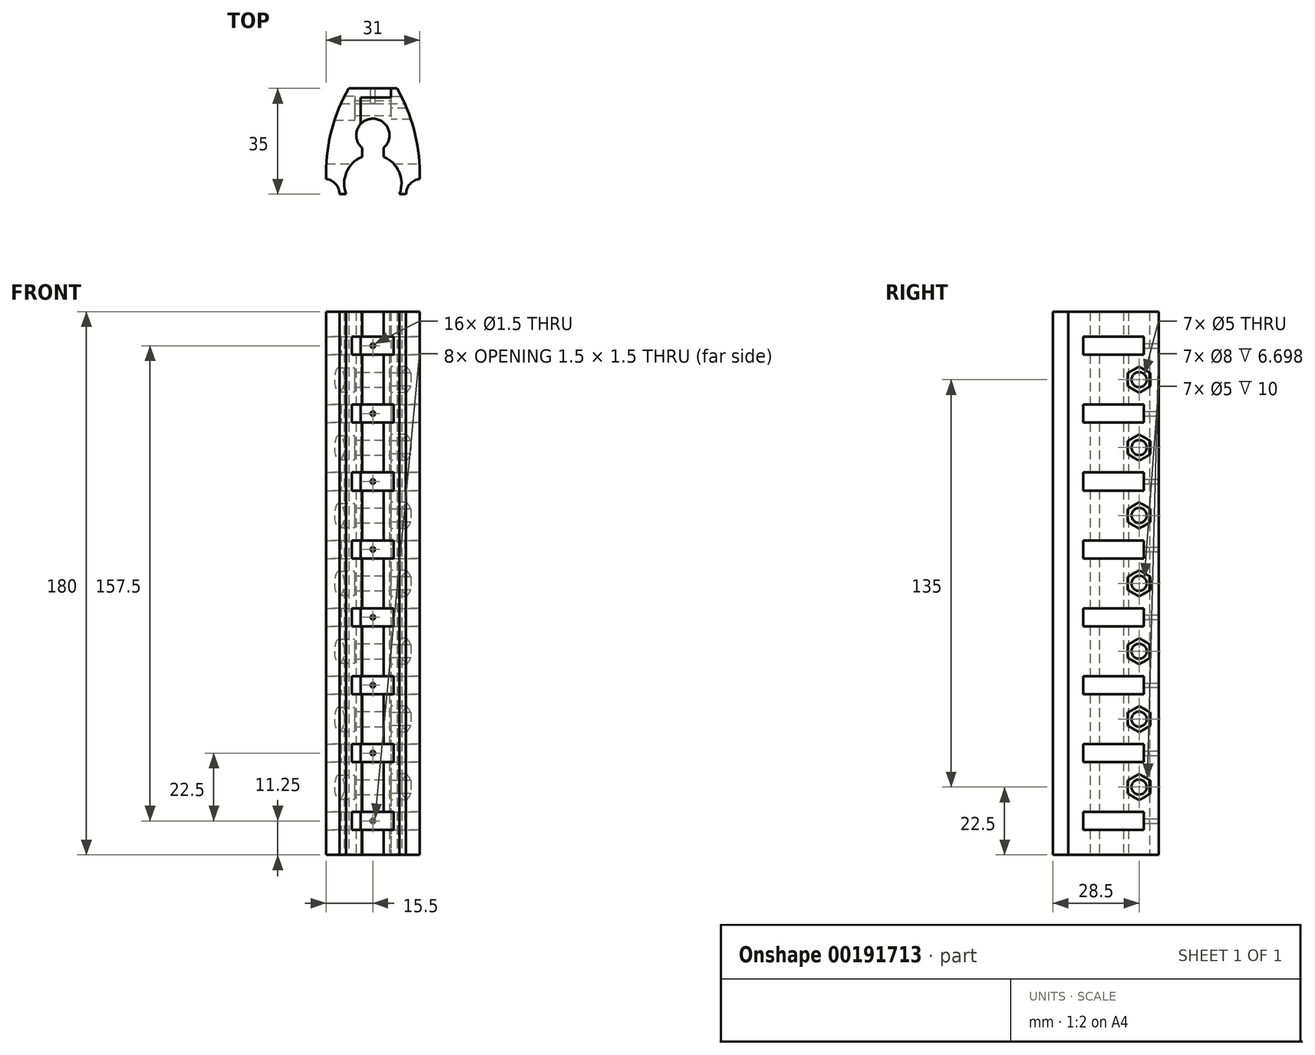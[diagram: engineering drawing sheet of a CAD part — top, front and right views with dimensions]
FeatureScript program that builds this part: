
annotation { "Feature Type Name" : "Feature", "Feature Type Description" : "" }
export const myFeature = defineFeature(function(context is Context, id is Id, definition is map)
    precondition{}
    {
        {
            var Q0;
            Q0=qCreatedBy(makeId("Top.planeOp"),FACE);
            var sketch = newSketch(context, id + "F0", { "sketchPlane" : qUnion([Q0])});
            skArc(sketch, "E0", {"start": v(3.56, -4.2) * mm, "mid": v(0, 5.5) * mm, "end": v(-3.56, -4.2) * mm});
            skArc(sketch, "E1", {"start": v(8.83, -19.5) * mm, "mid": v(8.73, -12.26) * mm, "end": v(3.56, -7.2) * mm});
            skLineSegment(sketch, "E2", {"start": v(-8.83, -19.5) * mm, "end": v(-11, -19.5) * mm});
            skLineSegment(sketch, "E3", {"start": v(-15.5, -14.53) * mm, "end": v(-15.5, -12.5) * mm});
            skLineSegment(sketch, "E4", {"start": v(-8, 15.5) * mm, "end": v(8, 15.5) * mm});
            skPoint(sketch, "E5", {"position": v(0, 15.5) * mm});
            skLineSegment(sketch, "E6", {"start": v(0, 30.37) * mm, "end": v(0, -34.56) * mm, "construction": true});
            skPoint(sketch, "E7", {"position": v(-15.5, -16) * mm});
            skArc(sketch, "E8", {"start": v(-8, 15.5) * mm, "mid": v(-13.6, 2) * mm, "end": v(-15.5, -12.5) * mm});
            skArc(sketch, "E9.MirrorCS", {"start": v(8, 15.5) * mm, "mid": v(13.6, 2) * mm, "end": v(15.5, -12.5) * mm});
            skLineSegment(sketch, "E10.MirrorCS", {"start": v(15.5, -14.53) * mm, "end": v(15.5, -12.5) * mm});
            skLineSegment(sketch, "E11.MirrorCS", {"start": v(8.83, -19.5) * mm, "end": v(11, -19.5) * mm});
            skLineSegment(sketch, "E12", {"start": v(-3.56, -4.2) * mm, "end": v(-3.56, -7.2) * mm});
            skLineSegment(sketch, "E13.MirrorCS", {"start": v(3.56, -4.2) * mm, "end": v(3.56, -7.2) * mm});
            skArc(sketch, "E14.trimOffspring", {"start": v(-3.56, -7.2) * mm, "mid": v(-8.73, -12.26) * mm, "end": v(-8.83, -19.5) * mm});
            skLineSegment(sketch, "E15", {"start": v(0, 15.5) * mm, "end": v(0, 5.5) * mm});
            skArc(sketch, "E16", {"start": v(-11, -19.5) * mm, "mid": v(-12.3, -16.15) * mm, "end": v(-15.5, -14.53) * mm});
            skArc(sketch, "E17", {"start": v(15.5, -14.53) * mm, "mid": v(12.3, -16.15) * mm, "end": v(11, -19.5) * mm});
            skPoint(sketch, "E18.orphan", {"position": v(15.5, -19.5) * mm});
            skPoint(sketch, "E19.orphan", {"position": v(-15.5, -19.5) * mm});
            skLineSegment(sketch, "E20", {"start": v(6, 15.5) * mm, "end": v(6, 12.5) * mm});
            skLineSegment(sketch, "E21", {"start": v(6, 12.5) * mm, "end": v(-4, 12.5) * mm});
            skLineSegment(sketch, "E22", {"start": v(-4, 12.5) * mm, "end": v(-4, 3.77) * mm});
            skSolve(sketch);
        }
        {
            var Q0;
            Q0=makeQuery(id+"F0.imprint","IMPRINT",FACE,{"disambiguationData":[TD([[makeQuery(id+"F0.imprint","IMPRINT",EDGE,{"derivedFrom":sQuery(id+"F0.wireOp",EDGE,"E1")}),-1.0]])]});
            var Q1;
            {var subQ3=sQuery(id+"F0.wireOp",EDGE,"E22");Q1=makeQuery(id+"F0.imprint","IMPRINT",FACE,{"disambiguationData":[TD([[makeQuery(id+"F0.imprint","IMPRINT",EDGE,{"derivedFrom":subQ3}),1.0]])]});}
            extrude(context, id + "F1", {"entities" : qUnion([Q0, Q1]), "depth" : 180 * mm});
        }
        {
            var Q0;
            Q0=makeQuery(id+"F0.imprint","IMPRINT",FACE,{"disambiguationData":[TD([[makeQuery(id+"F0.imprint","IMPRINT",EDGE,{"derivedFrom":sQuery(id+"F0.wireOp",EDGE,"E2")}),-1.0]])]});
            var Q1;
            {var subQ3=sQuery(id+"F0.wireOp",EDGE,"E20");Q1=makeQuery(id+"F0.imprint","IMPRINT",FACE,{"disambiguationData":[TD([[makeQuery(id+"F0.imprint","IMPRINT",EDGE,{"derivedFrom":subQ3}),-1.0]])]});}
            extrude(context, id + "F2", {"entities" : qUnion([Q0, Q1]), "depth" : 180 * mm});
        }
        {
            var Q0;
            Q0=qCreatedBy(makeId("Right.planeOp"),FACE);
            var sketch = newSketch(context, id + "F3", { "sketchPlane" : qUnion([Q0])});
            skCircle(sketch, "E23", {"center": v(9, 22.5) * mm, "radius": 2.5 * mm});
            skCircle(sketch, "E24", {"center": v(9, 45) * mm, "radius": 2.5 * mm});
            skCircle(sketch, "E25", {"center": v(9, 67.5) * mm, "radius": 2.5 * mm});
            skCircle(sketch, "E26", {"center": v(9, 90) * mm, "radius": 2.5 * mm});
            skCircle(sketch, "E27", {"center": v(9, 112.5) * mm, "radius": 2.5 * mm});
            skCircle(sketch, "E28", {"center": v(9, 135) * mm, "radius": 2.5 * mm});
            skCircle(sketch, "E29", {"center": v(9, 157.5) * mm, "radius": 2.5 * mm});
            skLineSegment(sketch, "E30", {"start": v(9, 22.5) * mm, "end": v(9, 157.5) * mm, "construction": true});
            skLineSegment(sketch, "E31", {"start": v(9, 90) * mm, "end": v(15.5, 90) * mm, "construction": true});
            skSolve(sketch);
        }
        {
            var Q0;
            Q0 = qSketchRegion(id + "F3", true);
            extrude(context, id + "F4", {"entities" : qUnion([Q0]), "operationType" : NewBodyOperationType.REMOVE, "endBound" : BoundingType.SYMMETRIC, "oppositeDirection" : true, "depth" : 100 * mm});
        }
        {
            var Q0;
            Q0=qCreatedBy(makeId("Right.planeOp"),FACE);
            var sketch = newSketch(context, id + "F5", { "sketchPlane" : qUnion([Q0])});
            skCircle(sketch, "E32", {"center": v(9, 22.5) * mm, "radius": 4 * mm});
            skCircle(sketch, "E33", {"center": v(9, 45) * mm, "radius": 4 * mm});
            skCircle(sketch, "E34", {"center": v(9, 67.5) * mm, "radius": 4 * mm});
            skCircle(sketch, "E35", {"center": v(9, 90) * mm, "radius": 4 * mm});
            skCircle(sketch, "E36", {"center": v(9, 112.5) * mm, "radius": 4 * mm});
            skCircle(sketch, "E37", {"center": v(9, 135) * mm, "radius": 4 * mm});
            skCircle(sketch, "E38", {"center": v(9, 157.5) * mm, "radius": 4 * mm});
            skSolve(sketch);
        }
        {
            var Q0;
            Q0 = qSketchRegion(id + "F5", true);
            extrude(context, id + "F6", {"entities" : qUnion([Q0]), "operationType" : NewBodyOperationType.REMOVE, "oppositeDirection" : true, "depth" : 45.7 * mm, "hasSecondDirection" : true, "secondDirectionOppositeDirection" : true, "secondDirectionDepth" : 6 * mm});
        }
        {
            var Q0;
            Q0=qCreatedBy(makeId("Right.planeOp"),FACE);
            var sketch = newSketch(context, id + "F7", { "sketchPlane" : qUnion([Q0])});
            skCircle(sketch, "E39.cCircle", {"center": v(9, 22.5) * mm, "radius": 3.75 * mm, "construction": true});
            skLineSegment(sketch, "E39.0", {"start": v(5.25, 20.33) * mm, "end": v(5.25, 24.67) * mm});
            skLineSegment(sketch, "E39.1", {"start": v(5.25, 24.67) * mm, "end": v(9, 26.83) * mm});
            skLineSegment(sketch, "E39.2", {"start": v(9, 26.83) * mm, "end": v(12.75, 24.67) * mm});
            skLineSegment(sketch, "E39.3", {"start": v(12.75, 24.67) * mm, "end": v(12.75, 20.33) * mm});
            skLineSegment(sketch, "E39.4", {"start": v(12.75, 20.33) * mm, "end": v(9, 18.17) * mm});
            skLineSegment(sketch, "E39.5", {"start": v(9, 18.17) * mm, "end": v(5.25, 20.33) * mm});
            skPoint(sketch, "E39.0.midPoint", {"position": v(5.25, 22.5) * mm});
            skCircle(sketch, "E40.cCircle", {"center": v(9, 45) * mm, "radius": 3.75 * mm, "construction": true});
            skLineSegment(sketch, "E40.0", {"start": v(5.25, 42.83) * mm, "end": v(5.25, 47.17) * mm});
            skLineSegment(sketch, "E40.1", {"start": v(5.25, 47.17) * mm, "end": v(9, 49.33) * mm});
            skLineSegment(sketch, "E40.2", {"start": v(9, 49.33) * mm, "end": v(12.75, 47.17) * mm});
            skLineSegment(sketch, "E40.3", {"start": v(12.75, 47.17) * mm, "end": v(12.75, 42.83) * mm});
            skLineSegment(sketch, "E40.4", {"start": v(12.75, 42.83) * mm, "end": v(9, 40.67) * mm});
            skLineSegment(sketch, "E40.5", {"start": v(9, 40.67) * mm, "end": v(5.25, 42.83) * mm});
            skPoint(sketch, "E40.0.midPoint", {"position": v(5.25, 45) * mm});
            skCircle(sketch, "E41.cCircle", {"center": v(9, 67.5) * mm, "radius": 3.75 * mm, "construction": true});
            skLineSegment(sketch, "E41.0", {"start": v(12.75, 69.67) * mm, "end": v(12.75, 65.33) * mm});
            skLineSegment(sketch, "E41.1", {"start": v(12.75, 65.33) * mm, "end": v(9, 63.17) * mm});
            skLineSegment(sketch, "E41.2", {"start": v(9, 63.17) * mm, "end": v(5.25, 65.33) * mm});
            skLineSegment(sketch, "E41.3", {"start": v(5.25, 65.33) * mm, "end": v(5.25, 69.67) * mm});
            skLineSegment(sketch, "E41.4", {"start": v(5.25, 69.67) * mm, "end": v(9, 71.83) * mm});
            skLineSegment(sketch, "E41.5", {"start": v(9, 71.83) * mm, "end": v(12.75, 69.67) * mm});
            skPoint(sketch, "E41.0.midPoint", {"position": v(12.75, 67.5) * mm});
            skCircle(sketch, "E42.cCircle", {"center": v(9, 90) * mm, "radius": 3.75 * mm, "construction": true});
            skLineSegment(sketch, "E42.0", {"start": v(12.75, 92.17) * mm, "end": v(12.75, 87.83) * mm});
            skLineSegment(sketch, "E42.1", {"start": v(12.75, 87.83) * mm, "end": v(9, 85.67) * mm});
            skLineSegment(sketch, "E42.2", {"start": v(9, 85.67) * mm, "end": v(5.25, 87.83) * mm});
            skLineSegment(sketch, "E42.3", {"start": v(5.25, 87.83) * mm, "end": v(5.25, 92.17) * mm});
            skLineSegment(sketch, "E42.4", {"start": v(5.25, 92.17) * mm, "end": v(9, 94.33) * mm});
            skLineSegment(sketch, "E42.5", {"start": v(9, 94.33) * mm, "end": v(12.75, 92.17) * mm});
            skPoint(sketch, "E42.0.midPoint", {"position": v(12.75, 90) * mm});
            skCircle(sketch, "E43.cCircle", {"center": v(9, 112.5) * mm, "radius": 3.75 * mm, "construction": true});
            skLineSegment(sketch, "E43.0", {"start": v(12.75, 114.67) * mm, "end": v(12.75, 110.33) * mm});
            skLineSegment(sketch, "E43.1", {"start": v(12.75, 110.33) * mm, "end": v(9, 108.17) * mm});
            skLineSegment(sketch, "E43.2", {"start": v(9, 108.17) * mm, "end": v(5.25, 110.33) * mm});
            skLineSegment(sketch, "E43.3", {"start": v(5.25, 110.33) * mm, "end": v(5.25, 114.67) * mm});
            skLineSegment(sketch, "E43.4", {"start": v(5.25, 114.67) * mm, "end": v(9, 116.83) * mm});
            skLineSegment(sketch, "E43.5", {"start": v(9, 116.83) * mm, "end": v(12.75, 114.67) * mm});
            skPoint(sketch, "E43.0.midPoint", {"position": v(12.75, 112.5) * mm});
            skCircle(sketch, "E44.cCircle", {"center": v(9, 135) * mm, "radius": 3.75 * mm, "construction": true});
            skLineSegment(sketch, "E44.0", {"start": v(5.25, 132.83) * mm, "end": v(5.25, 137.17) * mm});
            skLineSegment(sketch, "E44.1", {"start": v(5.25, 137.17) * mm, "end": v(9, 139.33) * mm});
            skLineSegment(sketch, "E44.2", {"start": v(9, 139.33) * mm, "end": v(12.75, 137.17) * mm});
            skLineSegment(sketch, "E44.3", {"start": v(12.75, 137.17) * mm, "end": v(12.75, 132.83) * mm});
            skLineSegment(sketch, "E44.4", {"start": v(12.75, 132.83) * mm, "end": v(9, 130.67) * mm});
            skLineSegment(sketch, "E44.5", {"start": v(9, 130.67) * mm, "end": v(5.25, 132.83) * mm});
            skPoint(sketch, "E44.0.midPoint", {"position": v(5.25, 135) * mm});
            skCircle(sketch, "E45.cCircle", {"center": v(9, 157.5) * mm, "radius": 3.75 * mm, "construction": true});
            skLineSegment(sketch, "E45.0", {"start": v(5.25, 155.33) * mm, "end": v(5.25, 159.67) * mm});
            skLineSegment(sketch, "E45.1", {"start": v(5.25, 159.67) * mm, "end": v(9, 161.83) * mm});
            skLineSegment(sketch, "E45.2", {"start": v(9, 161.83) * mm, "end": v(12.75, 159.67) * mm});
            skLineSegment(sketch, "E45.3", {"start": v(12.75, 159.67) * mm, "end": v(12.75, 155.33) * mm});
            skLineSegment(sketch, "E45.4", {"start": v(12.75, 155.33) * mm, "end": v(9, 153.17) * mm});
            skLineSegment(sketch, "E45.5", {"start": v(9, 153.17) * mm, "end": v(5.25, 155.33) * mm});
            skPoint(sketch, "E45.0.midPoint", {"position": v(5.25, 157.5) * mm});
            skSolve(sketch);
        }
        {
            var Q0;
            Q0 = qSketchRegion(id + "F7", true);
            extrude(context, id + "F8", {"entities" : qUnion([Q0]), "operationType" : NewBodyOperationType.REMOVE, "depth" : 87.7 * mm, "hasSecondDirection" : true, "secondDirectionOppositeDirection" : false, "secondDirectionDepth" : 6 * mm});
        }
        {
            var Q0;
            Q0=qCreatedBy(makeId("Right.planeOp"),FACE);
            var sketch = newSketch(context, id + "F9", { "sketchPlane" : qUnion([Q0])});
            skLineSegment(sketch, "E46.bottom", {"start": v(10.5, 165.75) * mm, "end": v(-9.5, 165.75) * mm});
            skLineSegment(sketch, "E46.top", {"start": v(10.5, 171.75) * mm, "end": v(-9.5, 171.75) * mm});
            skLineSegment(sketch, "E46.left", {"start": v(10.5, 165.75) * mm, "end": v(10.5, 171.75) * mm});
            skLineSegment(sketch, "E46.right", {"start": v(-9.5, 165.75) * mm, "end": v(-9.5, 171.75) * mm});
            skLineSegment(sketch, "E47.bottom", {"start": v(10.5, 143.25) * mm, "end": v(-9.5, 143.25) * mm});
            skLineSegment(sketch, "E47.top", {"start": v(10.5, 149.25) * mm, "end": v(-9.5, 149.25) * mm});
            skLineSegment(sketch, "E47.left", {"start": v(10.5, 143.25) * mm, "end": v(10.5, 149.25) * mm});
            skLineSegment(sketch, "E47.right", {"start": v(-9.5, 143.25) * mm, "end": v(-9.5, 149.25) * mm});
            skLineSegment(sketch, "E48.bottom", {"start": v(10.5, 120.75) * mm, "end": v(-9.5, 120.75) * mm});
            skLineSegment(sketch, "E48.top", {"start": v(10.5, 126.75) * mm, "end": v(-9.5, 126.75) * mm});
            skLineSegment(sketch, "E48.left", {"start": v(10.5, 120.75) * mm, "end": v(10.5, 126.75) * mm});
            skLineSegment(sketch, "E48.right", {"start": v(-9.5, 120.75) * mm, "end": v(-9.5, 126.75) * mm});
            skLineSegment(sketch, "E49.bottom", {"start": v(10.5, 98.25) * mm, "end": v(-9.5, 98.25) * mm});
            skLineSegment(sketch, "E49.top", {"start": v(10.5, 104.25) * mm, "end": v(-9.5, 104.25) * mm});
            skLineSegment(sketch, "E49.left", {"start": v(10.5, 98.25) * mm, "end": v(10.5, 104.25) * mm});
            skLineSegment(sketch, "E49.right", {"start": v(-9.5, 98.25) * mm, "end": v(-9.5, 104.25) * mm});
            skLineSegment(sketch, "E50.bottom", {"start": v(10.5, 75.75) * mm, "end": v(-9.5, 75.75) * mm});
            skLineSegment(sketch, "E50.top", {"start": v(10.5, 81.75) * mm, "end": v(-9.5, 81.75) * mm});
            skLineSegment(sketch, "E50.left", {"start": v(10.5, 75.75) * mm, "end": v(10.5, 81.75) * mm});
            skLineSegment(sketch, "E50.right", {"start": v(-9.5, 75.75) * mm, "end": v(-9.5, 81.75) * mm});
            skLineSegment(sketch, "E51.bottom", {"start": v(10.5, 53.25) * mm, "end": v(-9.5, 53.25) * mm});
            skLineSegment(sketch, "E51.top", {"start": v(10.5, 59.25) * mm, "end": v(-9.5, 59.25) * mm});
            skLineSegment(sketch, "E51.left", {"start": v(10.5, 53.25) * mm, "end": v(10.5, 59.25) * mm});
            skLineSegment(sketch, "E51.right", {"start": v(-9.5, 53.25) * mm, "end": v(-9.5, 59.25) * mm});
            skLineSegment(sketch, "E52.bottom", {"start": v(10.5, 30.75) * mm, "end": v(-9.5, 30.75) * mm});
            skLineSegment(sketch, "E52.top", {"start": v(10.5, 36.75) * mm, "end": v(-9.5, 36.75) * mm});
            skLineSegment(sketch, "E52.left", {"start": v(10.5, 30.75) * mm, "end": v(10.5, 36.75) * mm});
            skLineSegment(sketch, "E52.right", {"start": v(-9.5, 30.75) * mm, "end": v(-9.5, 36.75) * mm});
            skLineSegment(sketch, "E53.bottom", {"start": v(10.5, 8.25) * mm, "end": v(-9.5, 8.25) * mm});
            skLineSegment(sketch, "E53.top", {"start": v(10.5, 14.25) * mm, "end": v(-9.5, 14.25) * mm});
            skLineSegment(sketch, "E53.left", {"start": v(10.5, 8.25) * mm, "end": v(10.5, 14.25) * mm});
            skLineSegment(sketch, "E53.right", {"start": v(-9.5, 8.25) * mm, "end": v(-9.5, 14.25) * mm});
            skLineSegment(sketch, "E54", {"start": v(-27.58, 157.5) * mm, "end": v(57.25, 157.5) * mm, "construction": true});
            skLineSegment(sketch, "E55", {"start": v(59.34, 135) * mm, "end": v(-46.34, 135) * mm, "construction": true});
            skLineSegment(sketch, "E56", {"start": v(-38.3, 112.5) * mm, "end": v(56.96, 112.5) * mm, "construction": true});
            skLineSegment(sketch, "E57", {"start": v(50.4, 90) * mm, "end": v(-40.68, 90) * mm, "construction": true});
            skLineSegment(sketch, "E58", {"start": v(-37.4, 67.5) * mm, "end": v(56.36, 67.5) * mm, "construction": true});
            skLineSegment(sketch, "E59", {"start": v(56.36, 45) * mm, "end": v(-40.38, 45) * mm, "construction": true});
            skLineSegment(sketch, "E60", {"start": v(-35.92, 22.5) * mm, "end": v(51.9, 22.5) * mm, "construction": true});
            skPoint(sketch, "E61", {"position": v(10.5, 168.75) * mm});
            skPoint(sketch, "E62", {"position": v(10.5, 146.25) * mm});
            skPoint(sketch, "E63", {"position": v(10.5, 123.75) * mm});
            skPoint(sketch, "E64", {"position": v(10.5, 101.25) * mm});
            skPoint(sketch, "E65", {"position": v(10.5, 78.75) * mm});
            skPoint(sketch, "E66", {"position": v(10.5, 56.25) * mm});
            skPoint(sketch, "E67", {"position": v(10.5, 33.75) * mm});
            skPoint(sketch, "E68", {"position": v(10.5, 11.25) * mm});
            skLineSegment(sketch, "E69", {"start": v(-36.06, 180) * mm, "end": v(81.42, 180) * mm, "construction": true});
            skLineSegment(sketch, "E70", {"start": v(44.03, 180) * mm, "end": v(44.03, 157.5) * mm, "construction": true});
            skPoint(sketch, "E71", {"position": v(44.03, 168.75) * mm});
            skSolve(sketch);
        }
        {
            var Q0;
            Q0 = qSketchRegion(id + "F9", true);
            extrude(context, id + "F10", {"entities" : qUnion([Q0]), "operationType" : NewBodyOperationType.REMOVE, "endBound" : BoundingType.SYMMETRIC, "oppositeDirection" : true, "depth" : 50 * mm});
        }
        {
            var Q0;
            Q0=makeQuery(id+"F2.opExtrude","SWEPT_FACE",FACE,{"disambiguationData":[OSD([sQuery(id+"F0.wireOp",EDGE,"E4")])]});
            var sketch = newSketch(context, id + "F11", { "sketchPlane" : qUnion([Q0])});
            skCircle(sketch, "E72", {"center": v(0, 168.75) * mm, "radius": 0.75 * mm});
            skCircle(sketch, "E73", {"center": v(0, 146.25) * mm, "radius": 0.75 * mm});
            skCircle(sketch, "E74", {"center": v(0, 123.75) * mm, "radius": 0.75 * mm});
            skCircle(sketch, "E75", {"center": v(0, 101.25) * mm, "radius": 0.75 * mm});
            skCircle(sketch, "E76", {"center": v(0, 78.75) * mm, "radius": 0.75 * mm});
            skCircle(sketch, "E77", {"center": v(0, 56.25) * mm, "radius": 0.75 * mm});
            skCircle(sketch, "E78", {"center": v(0, 33.75) * mm, "radius": 0.75 * mm});
            skCircle(sketch, "E79", {"center": v(0, 11.25) * mm, "radius": 0.75 * mm});
            skSolve(sketch);
        }
        {
            var Q0;
            Q0 = qSketchRegion(id + "F11", true);
            extrude(context, id + "F12", {"entities" : qUnion([Q0]), "operationType" : NewBodyOperationType.REMOVE, "oppositeDirection" : true, "depth" : 25 * mm});
        }
    });
